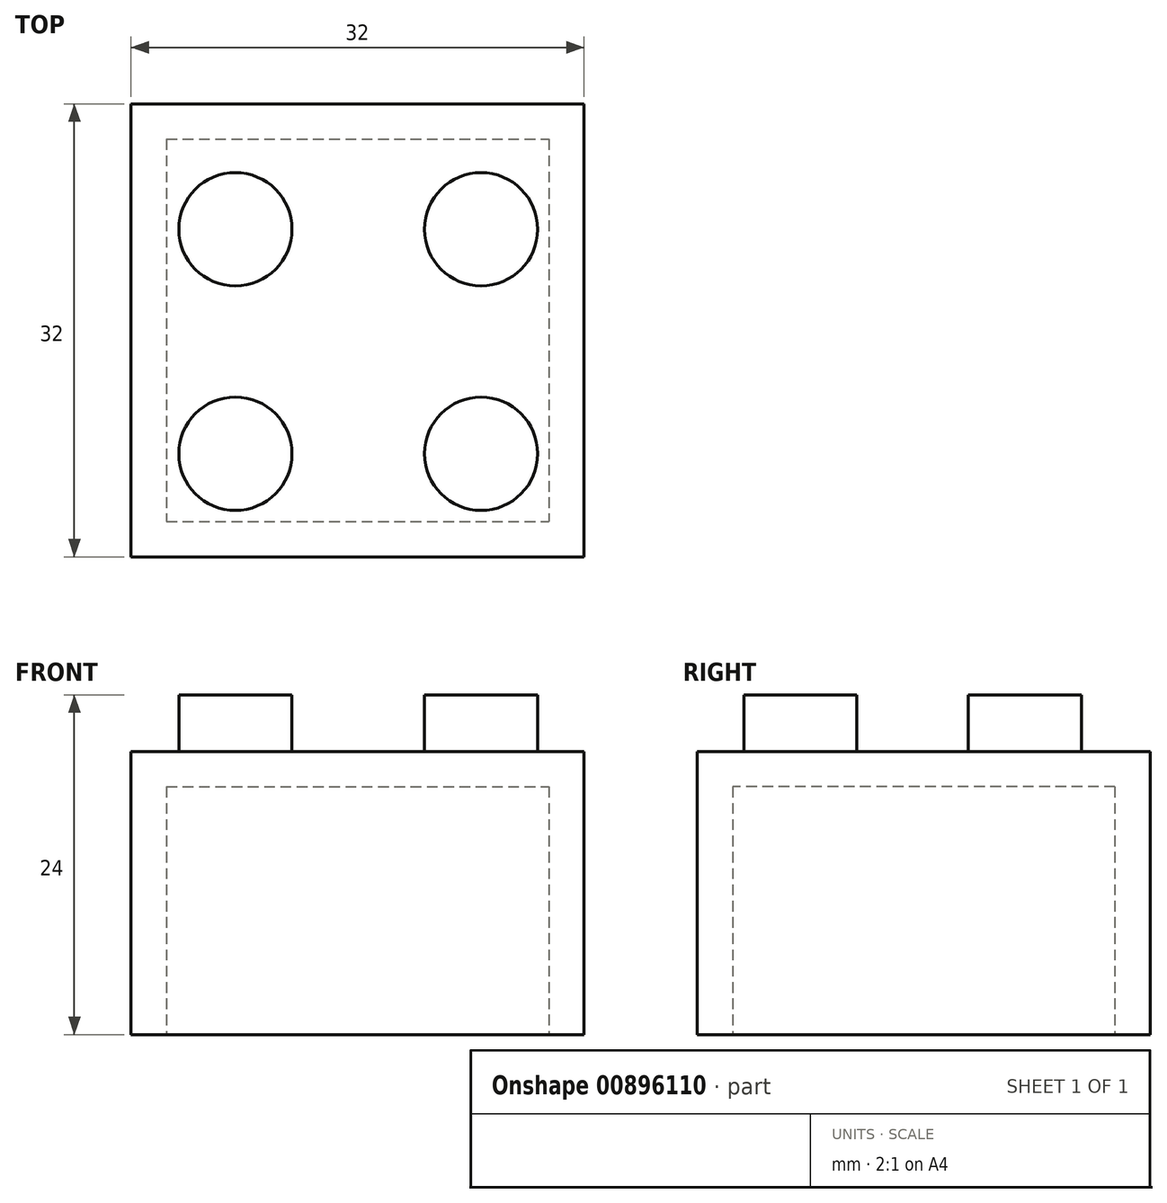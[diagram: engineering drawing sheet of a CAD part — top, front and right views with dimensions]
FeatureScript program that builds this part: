
annotation { "Feature Type Name" : "Feature", "Feature Type Description" : "" }
export const myFeature = defineFeature(function(context is Context, id is Id, definition is map)
    precondition{}
    {
        {
            var Q0;
            Q0=qCreatedBy(makeId("Top.planeOp"),FACE);
            var sketch = newSketch(context, id + "F0", { "sketchPlane" : qUnion([Q0])});
            skLineSegment(sketch, "E0.bottom", {"start": v(-56.73, 41.98) * mm, "end": v(-24.73, 41.98) * mm});
            skLineSegment(sketch, "E0.top", {"start": v(-56.73, 9.98) * mm, "end": v(-24.73, 9.98) * mm});
            skLineSegment(sketch, "E0.left", {"start": v(-56.73, 41.98) * mm, "end": v(-56.73, 9.98) * mm});
            skLineSegment(sketch, "E0.right", {"start": v(-24.73, 41.98) * mm, "end": v(-24.73, 9.98) * mm});
            skSolve(sketch);
        }
        {
            var Q0;
            Q0=makeQuery(id+"F0.imprint","IMPRINT",FACE,{"disambiguationData":[TD([[makeQuery(id+"F0.imprint","IMPRINT",EDGE,{"derivedFrom":sQuery(id+"F0.wireOp",EDGE,"E0.bottom")}),-1.0]])]});
            extrude(context, id + "F1", {"entities" : qUnion([Q0]), "depth" : 20 * mm, "offsetDistance" : 25 * mm});
        }
        {
            var Q0;
            Q0=makeQuery(id+"F1.opExtrude","CAP_FACE",FACE,{"disambiguationData":[OSD([sQuery(id+"F0.wireOp",EDGE,"E0.bottom"),sQuery(id+"F0.wireOp",EDGE,"E0.top"),sQuery(id+"F0.wireOp",EDGE,"E0.left"),sQuery(id+"F0.wireOp",EDGE,"E0.right")])],"isStart":true});
            shell(context, id + "F2", {"entities" : qUnion([Q0]), "thickness" : 2.5 * mm});
        }
        {
            var Q0;
            Q0=makeQuery(id+"F1.opExtrude","CAP_FACE",FACE,{"disambiguationData":[OSD([sQuery(id+"F0.wireOp",EDGE,"E0.bottom"),sQuery(id+"F0.wireOp",EDGE,"E0.top"),sQuery(id+"F0.wireOp",EDGE,"E0.left"),sQuery(id+"F0.wireOp",EDGE,"E0.right")])],"isStart":false});
            var sketch = newSketch(context, id + "F3", { "sketchPlane" : qUnion([Q0])});
            skCircle(sketch, "E1", {"center": v(-49.36, 33.12) * mm, "radius": 4 * mm});
            skCircle(sketch, "E2", {"center": v(-49.36, 17.26) * mm, "radius": 4 * mm});
            skCircle(sketch, "E3", {"center": v(-32, 17.26) * mm, "radius": 4 * mm});
            skCircle(sketch, "E4", {"center": v(-32, 33.12) * mm, "radius": 4 * mm});
            skSolve(sketch);
        }
        {
            var Q0;
            Q0=makeQuery(id+"F3.imprint","IMPRINT",FACE,{"disambiguationData":[TD([[makeQuery(id+"F3.imprint","IMPRINT",EDGE,{"derivedFrom":sQuery(id+"F3.wireOp",EDGE,"E1")}),1.0]])]});
            var Q1;
            Q1=makeQuery(id+"F3.imprint","IMPRINT",FACE,{"disambiguationData":[TD([[makeQuery(id+"F3.imprint","IMPRINT",EDGE,{"derivedFrom":sQuery(id+"F3.wireOp",EDGE,"E2")}),1.0]])]});
            var Q2;
            Q2=makeQuery(id+"F3.imprint","IMPRINT",FACE,{"disambiguationData":[TD([[makeQuery(id+"F3.imprint","IMPRINT",EDGE,{"derivedFrom":sQuery(id+"F3.wireOp",EDGE,"E3")}),1.0]])]});
            var Q3;
            Q3=makeQuery(id+"F3.imprint","IMPRINT",FACE,{"disambiguationData":[TD([[makeQuery(id+"F3.imprint","IMPRINT",EDGE,{"derivedFrom":sQuery(id+"F3.wireOp",EDGE,"E4")}),1.0]])]});
            extrude(context, id + "F4", {"entities" : qUnion([Q0, Q1, Q2, Q3]), "operationType" : NewBodyOperationType.ADD, "depth" : 4 * mm, "offsetDistance" : 25 * mm});
        }
    });
